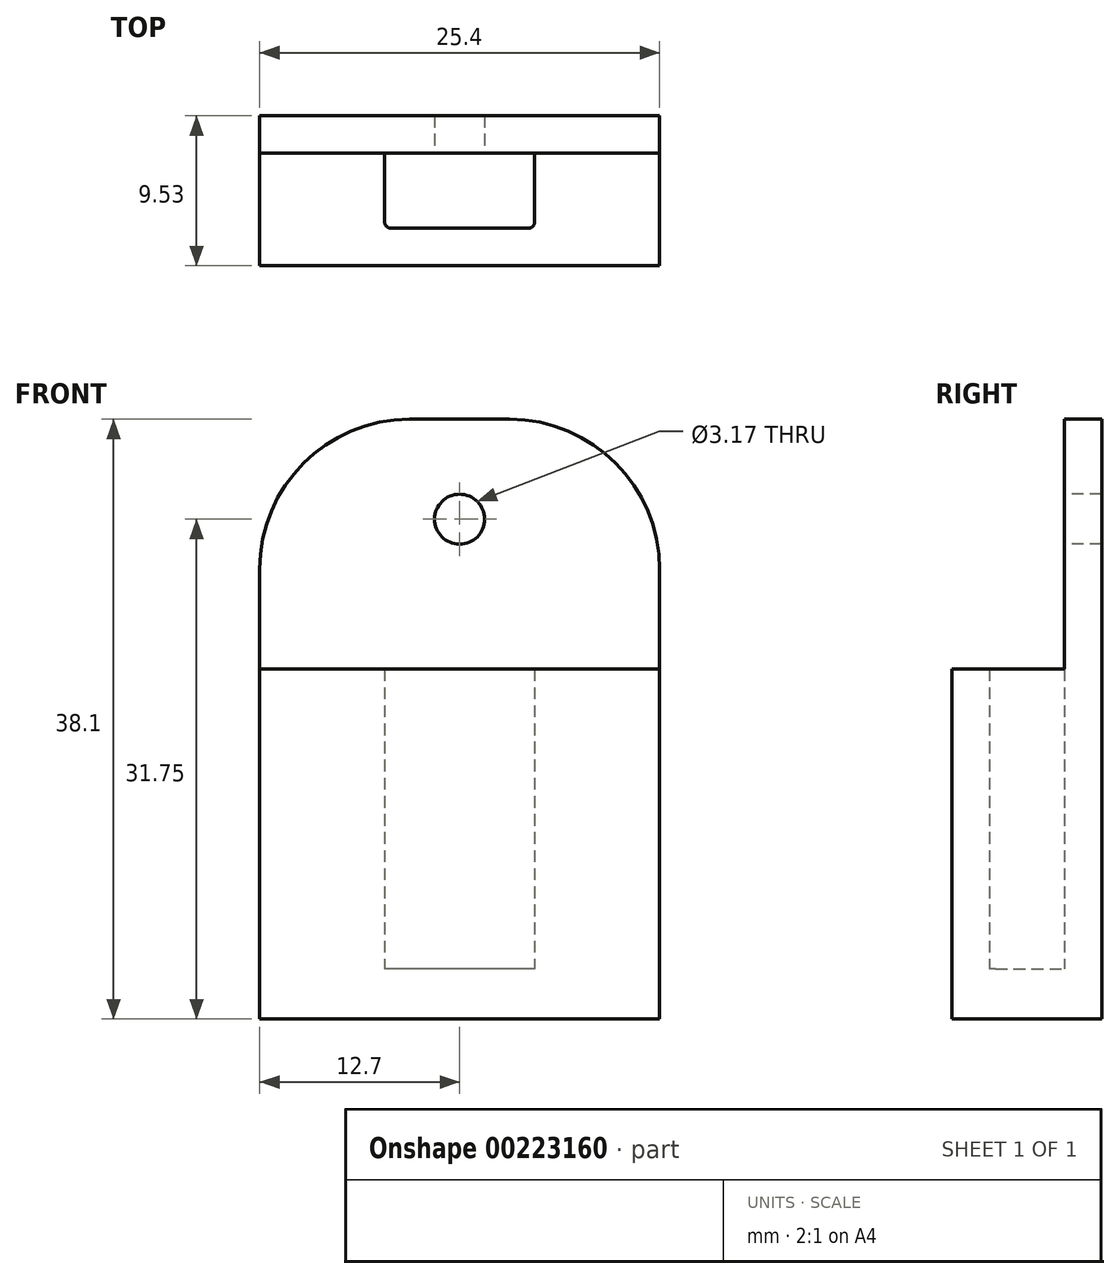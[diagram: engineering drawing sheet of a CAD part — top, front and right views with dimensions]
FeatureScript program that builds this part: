
annotation { "Feature Type Name" : "Feature", "Feature Type Description" : "" }
export const myFeature = defineFeature(function(context is Context, id is Id, definition is map)
    precondition{}
    {
        {
            var Q0;
            Q0=qCreatedBy(makeId("Front.planeOp"),FACE);
            var sketch = newSketch(context, id + "F0", { "sketchPlane" : qUnion([Q0])});
            skLineSegment(sketch, "E0.bottom", {"start": v(-12.7, 0) * mm, "end": v(12.7, 0) * mm});
            skLineSegment(sketch, "E0.top", {"start": v(-12.7, 38.1) * mm, "end": v(12.7, 38.1) * mm});
            skLineSegment(sketch, "E0.left", {"start": v(-12.7, 0) * mm, "end": v(-12.7, 38.1) * mm});
            skLineSegment(sketch, "E0.right", {"start": v(12.7, 0) * mm, "end": v(12.7, 38.1) * mm});
            skSolve(sketch);
        }
        {
            var Q0;
            Q0=makeQuery(id+"F0.imprint","IMPRINT",FACE,{"disambiguationData":[TD([[makeQuery(id+"F0.imprint","IMPRINT",EDGE,{"derivedFrom":sQuery(id+"F0.wireOp",EDGE,"E0.bottom")}),1.0]])]});
            extrude(context, id + "F1", {"entities" : qUnion([Q0]), "depth" : 9.52 * mm});
        }
        {
            var Q0;
            Q0=qCreatedBy(makeId("Top.planeOp"),FACE);
            var sketch = newSketch(context, id + "F2", { "sketchPlane" : qUnion([Q0])});
            skLineSegment(sketch, "E1.bottom", {"start": v(-4.76, -2.38) * mm, "end": v(4.76, -2.38) * mm});
            skLineSegment(sketch, "E1.top", {"start": v(-4.76, -7.14) * mm, "end": v(4.76, -7.14) * mm});
            skLineSegment(sketch, "E1.left", {"start": v(-4.76, -2.38) * mm, "end": v(-4.76, -7.14) * mm});
            skLineSegment(sketch, "E1.right", {"start": v(4.76, -2.38) * mm, "end": v(4.76, -7.14) * mm});
            skLineSegment(sketch, "E2.bottom", {"start": v(-1.98, -7.14) * mm, "end": v(1.98, -7.14) * mm});
            skLineSegment(sketch, "E2.top", {"start": v(-1.98, -9.53) * mm, "end": v(1.98, -9.53) * mm});
            skLineSegment(sketch, "E2.left", {"start": v(-1.98, -7.14) * mm, "end": v(-1.98, -9.53) * mm});
            skLineSegment(sketch, "E2.right", {"start": v(1.98, -7.14) * mm, "end": v(1.98, -9.53) * mm});
            skSolve(sketch);
        }
        {
            var Q0;
            Q0=makeQuery(id+"F2.imprint","IMPRINT",FACE,{"disambiguationData":[TD([[makeQuery(id+"F2.imprint","IMPRINT",EDGE,{"derivedFrom":sQuery(id+"F2.wireOp",EDGE,"E1.bottom")}),-1.0]])]});
            var Q1;
            Q1=makeQuery(id+"F2.imprint","IMPRINT",FACE,{"disambiguationData":[TD([[makeQuery(id+"F2.imprint","IMPRINT",EDGE,{"derivedFrom":sQuery(id+"F2.wireOp",EDGE,"E2.bottom")}),-1.0]])]});
            var Q2;
            Q2=makeQuery(id+"FwwtnFH6q7YKgXq_1.boolean.opBoolean","COPY",FACE,{"derivedFrom":makeQuery(id+"FwwtnFH6q7YKgXq_1.opExtrude","SWEPT_FACE",FACE,{"disambiguationData":[OSD([sQuery(id+"FvvoTELVohwJk8I_1.wireOp",EDGE,"44IcOOyf-7ZrF-27Yc-bIAn-iyFCWgn7fINv.top")])]})});
            extrude(context, id + "F3", {"entities" : qUnion([Q0, Q1]), "operationType" : NewBodyOperationType.REMOVE, "endBoundEntityFace" : qUnion([Q2]), "depth" : 22.22 * mm});
        }
        {
            var Q0;
            Q0=makeQuery(id+"F1.opExtrude","CAP_FACE",FACE,{"disambiguationData":[OSD([sQuery(id+"F0.wireOp",EDGE,"E0.bottom"),sQuery(id+"F0.wireOp",EDGE,"E0.top"),sQuery(id+"F0.wireOp",EDGE,"E0.left"),sQuery(id+"F0.wireOp",EDGE,"E0.right")])],"isStart":false});
            var sketch = newSketch(context, id + "F4", { "sketchPlane" : qUnion([Q0])});
            skLineSegment(sketch, "E3.bottom", {"start": v(-12.7, 38.1) * mm, "end": v(12.7, 38.1) * mm});
            skLineSegment(sketch, "E3.top", {"start": v(-12.7, 22.23) * mm, "end": v(12.7, 22.23) * mm});
            skLineSegment(sketch, "E3.left", {"start": v(-12.7, 38.1) * mm, "end": v(-12.7, 22.23) * mm});
            skLineSegment(sketch, "E3.right", {"start": v(12.7, 38.1) * mm, "end": v(12.7, 22.23) * mm});
            skSolve(sketch);
        }
        {
            var Q0;
            Q0=makeQuery(id+"F4.imprint","IMPRINT",FACE,{"disambiguationData":[TD([[makeQuery(id+"F4.imprint","IMPRINT",EDGE,{"derivedFrom":sQuery(id+"F4.wireOp",EDGE,"E3.bottom")}),-1.0]])]});
            extrude(context, id + "F5", {"entities" : qUnion([Q0]), "operationType" : NewBodyOperationType.REMOVE, "oppositeDirection" : true, "depth" : 7.14 * mm});
        }
        {
            var Q0;
            Q0=makeQuery(id+"F1.opExtrude","SWEPT_EDGE",EDGE,{"disambiguationData":[OSD([sQuery(id+"F0.wireOp",EDGE,"E0.top"),sQuery(id+"F0.wireOp",EDGE,"E0.right")])]});
            var Q1;
            Q1=makeQuery(id+"F1.opExtrude","SWEPT_EDGE",EDGE,{"disambiguationData":[OSD([sQuery(id+"F0.wireOp",EDGE,"E0.top"),sQuery(id+"F0.wireOp",EDGE,"E0.left")])]});
            fillet(context, id + "F6", {"entities" : qUnion([Q0, Q1]), "radius" : 9.52 * mm, "tangentPropagation" : true, "allowEdgeOverflow" : false});
        }
        {
            var Q0;
            Q0=makeQuery(id+"F3.boolean.opBoolean","COPY",EDGE,{"derivedFrom":makeQuery(id+"F3.opExtrude","SWEPT_EDGE",EDGE,{"disambiguationData":[OSD([sQuery(id+"F2.wireOp",EDGE,"E1.top"),sQuery(id+"F2.wireOp",EDGE,"E1.left")])]})});
            var Q1;
            Q1=makeQuery(id+"F3.boolean.opBoolean","COPY",EDGE,{"derivedFrom":makeQuery(id+"F3.opExtrude","SWEPT_EDGE",EDGE,{"disambiguationData":[OSD([sQuery(id+"F2.wireOp",EDGE,"E1.top"),sQuery(id+"F2.wireOp",EDGE,"E1.right")])]})});
            var Q2;
            Q2=makeQuery(id+"F3.boolean.opBoolean","COPY",EDGE,{"derivedFrom":makeQuery(id+"F3.opExtrude","SWEPT_EDGE",EDGE,{"disambiguationData":[OSD([sQuery(id+"F2.wireOp",EDGE,"E1.top"),sQuery(id+"F2.wireOp",EDGE,"E2.bottom"),sQuery(id+"F2.wireOp",EDGE,"E2.right")])]})});
            var Q3;
            Q3=makeQuery(id+"F3.boolean.opBoolean","COPY",EDGE,{"derivedFrom":makeQuery(id+"F3.opExtrude","SWEPT_EDGE",EDGE,{"disambiguationData":[OSD([sQuery(id+"F2.wireOp",EDGE,"E2.top"),sQuery(id+"F2.wireOp",EDGE,"E2.right")])]})});
            var Q4;
            Q4=makeQuery(id+"F3.boolean.opBoolean","COPY",EDGE,{"derivedFrom":makeQuery(id+"F3.opExtrude","SWEPT_EDGE",EDGE,{"disambiguationData":[OSD([sQuery(id+"F2.wireOp",EDGE,"E1.top"),sQuery(id+"F2.wireOp",EDGE,"E2.bottom"),sQuery(id+"F2.wireOp",EDGE,"E2.left")])]})});
            var Q5;
            Q5=makeQuery(id+"F3.boolean.opBoolean","COPY",EDGE,{"derivedFrom":makeQuery(id+"F3.opExtrude","SWEPT_EDGE",EDGE,{"disambiguationData":[OSD([sQuery(id+"F2.wireOp",EDGE,"E2.top"),sQuery(id+"F2.wireOp",EDGE,"E2.left")])]})});
            fillet(context, id + "F7", {"entities" : qUnion([Q0, Q1, Q2, Q3, Q4, Q5]), "radius" : 0.4 * mm, "tangentPropagation" : true, "allowEdgeOverflow" : false});
        }
        {
            var Q0;
            Q0=makeQuery(id+"F1.opExtrude","SWEPT_FACE",FACE,{"disambiguationData":[OSD([sQuery(id+"F0.wireOp",EDGE,"E0.bottom")])]});
            var sketch = newSketch(context, id + "F8", { "sketchPlane" : qUnion([Q0])});
            skLineSegment(sketch, "E4.bottom", {"start": v(-12.7, 9.53) * mm, "end": v(12.7, 9.53) * mm});
            skLineSegment(sketch, "E4.top", {"start": v(-12.7, 0) * mm, "end": v(12.7, 0) * mm});
            skLineSegment(sketch, "E4.left", {"start": v(-12.7, 9.53) * mm, "end": v(-12.7, 0) * mm});
            skLineSegment(sketch, "E4.right", {"start": v(12.7, 9.53) * mm, "end": v(12.7, 0) * mm});
            skSolve(sketch);
        }
        {
            var Q0;
            Q0 = qSketchRegion(id + "F8", true);
            extrude(context, id + "F9", {"entities" : qUnion([Q0]), "operationType" : NewBodyOperationType.ADD, "oppositeDirection" : true, "depth" : 3.17 * mm});
        }
        {
            var Q0;
            Q0=makeQuery(id+"F5.boolean.opBoolean","MERGE",FACE,{"derivedFrom":[makeQuery(id+"F3.boolean.opBoolean","COPY",FACE,{"derivedFrom":makeQuery(id+"F3.opExtrude","SWEPT_FACE",FACE,{"disambiguationData":[OSD([sQuery(id+"F2.wireOp",EDGE,"E1.bottom")])]})}),makeQuery(id+"F5.opExtrude","CAP_FACE",FACE,{"disambiguationData":[OSD([sQuery(id+"F4.wireOp",EDGE,"E3.bottom"),sQuery(id+"F4.wireOp",EDGE,"E3.top"),sQuery(id+"F4.wireOp",EDGE,"E3.left"),sQuery(id+"F4.wireOp",EDGE,"E3.right")])],"isStart":false})]});
            var sketch = newSketch(context, id + "F10", { "sketchPlane" : qUnion([Q0])});
            skCircle(sketch, "E5", {"center": v(0, 31.75) * mm, "radius": 1.59 * mm});
            skSolve(sketch);
        }
        {
            var Q0;
            Q0=makeQuery(id+"F10.imprint","IMPRINT",FACE,{"disambiguationData":[TD([[makeQuery(id+"F10.imprint","IMPRINT",EDGE,{"derivedFrom":sQuery(id+"F10.wireOp",EDGE,"E5")}),1.0]])]});
            extrude(context, id + "F11", {"entities" : qUnion([Q0]), "operationType" : NewBodyOperationType.REMOVE, "endBound" : BoundingType.THROUGH_ALL, "oppositeDirection" : true, "depth" : 25.4 * mm});
        }
    });
